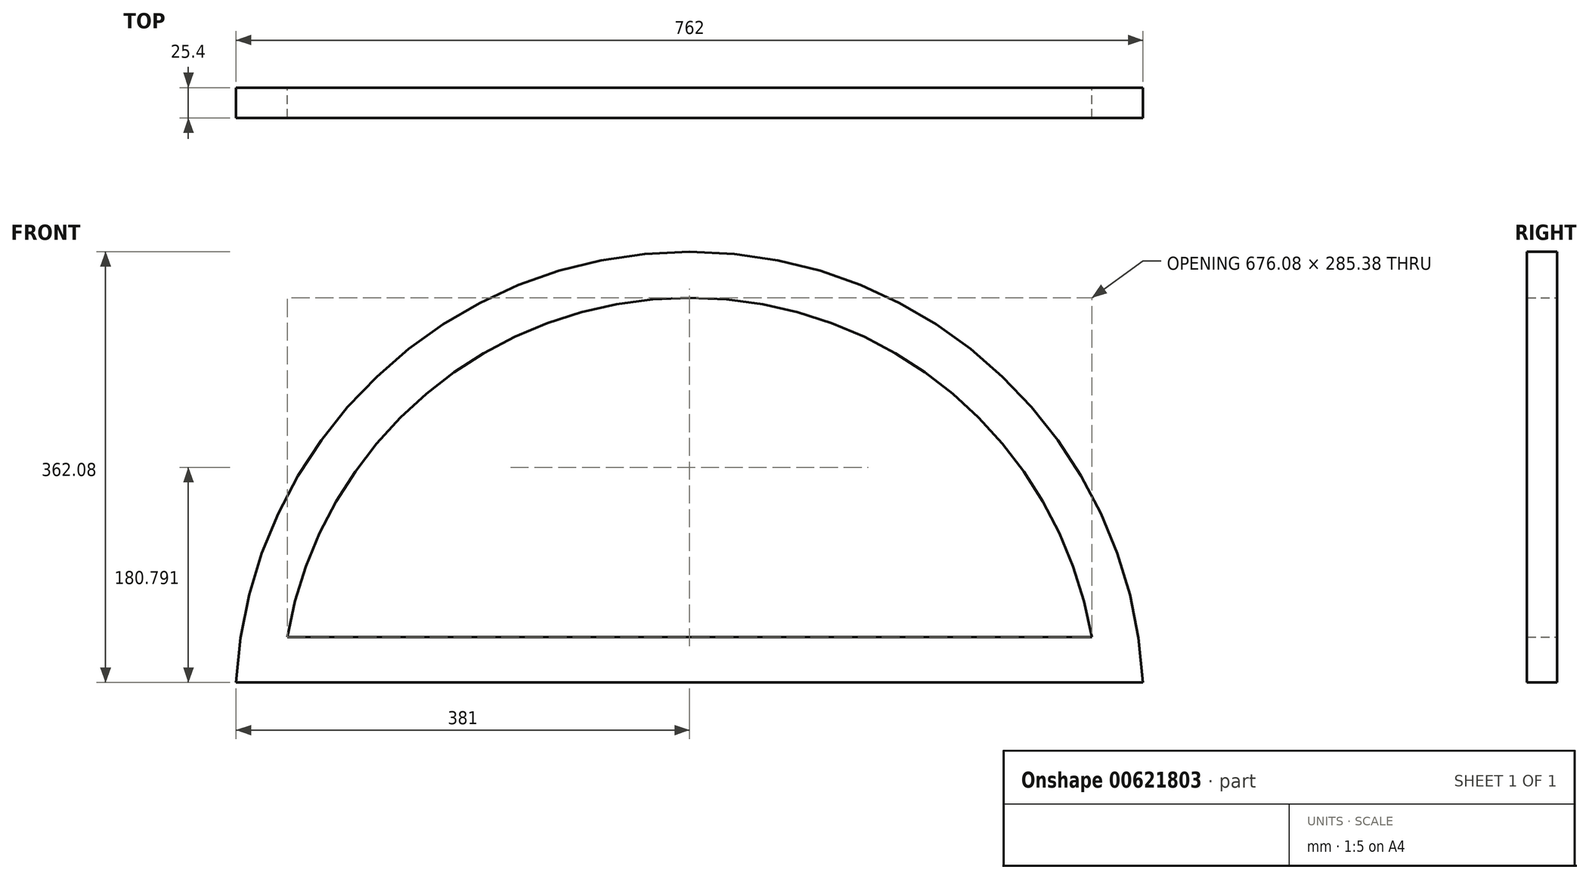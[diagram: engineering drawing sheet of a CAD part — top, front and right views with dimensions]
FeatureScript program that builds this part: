
annotation { "Feature Type Name" : "Feature", "Feature Type Description" : "" }
export const myFeature = defineFeature(function(context is Context, id is Id, definition is map)
    precondition{}
    {
        {
            var Q0;
            Q0=qCreatedBy(makeId("Front.planeOp"),FACE);
            var sketch = newSketch(context, id + "F0", { "sketchPlane" : qUnion([Q0])});
            skLineSegment(sketch, "E0", {"start": v(-381, 0) * mm, "end": v(381, 0) * mm});
            skArc(sketch, "E1", {"start": v(381, 0) * mm, "mid": v(0, 362.08) * mm, "end": v(-381, 0) * mm});
            skLineSegment(sketch, "E2", {"start": v(-338.04, 38.1) * mm, "end": v(338.04, 38.1) * mm});
            skArc(sketch, "E3.trimOffspring", {"start": v(338.04, 38.1) * mm, "mid": v(0, 323.48) * mm, "end": v(-338.04, 38.1) * mm});
            skSolve(sketch);
        }
        {
            var Q0;
            Q0 = qSketchRegion(id + "F0", true);
            extrude(context, id + "F1", {"entities" : qUnion([Q0]), "depth" : 25.4 * mm, "offsetDistance" : 25.4 * mm});
        }
    });
